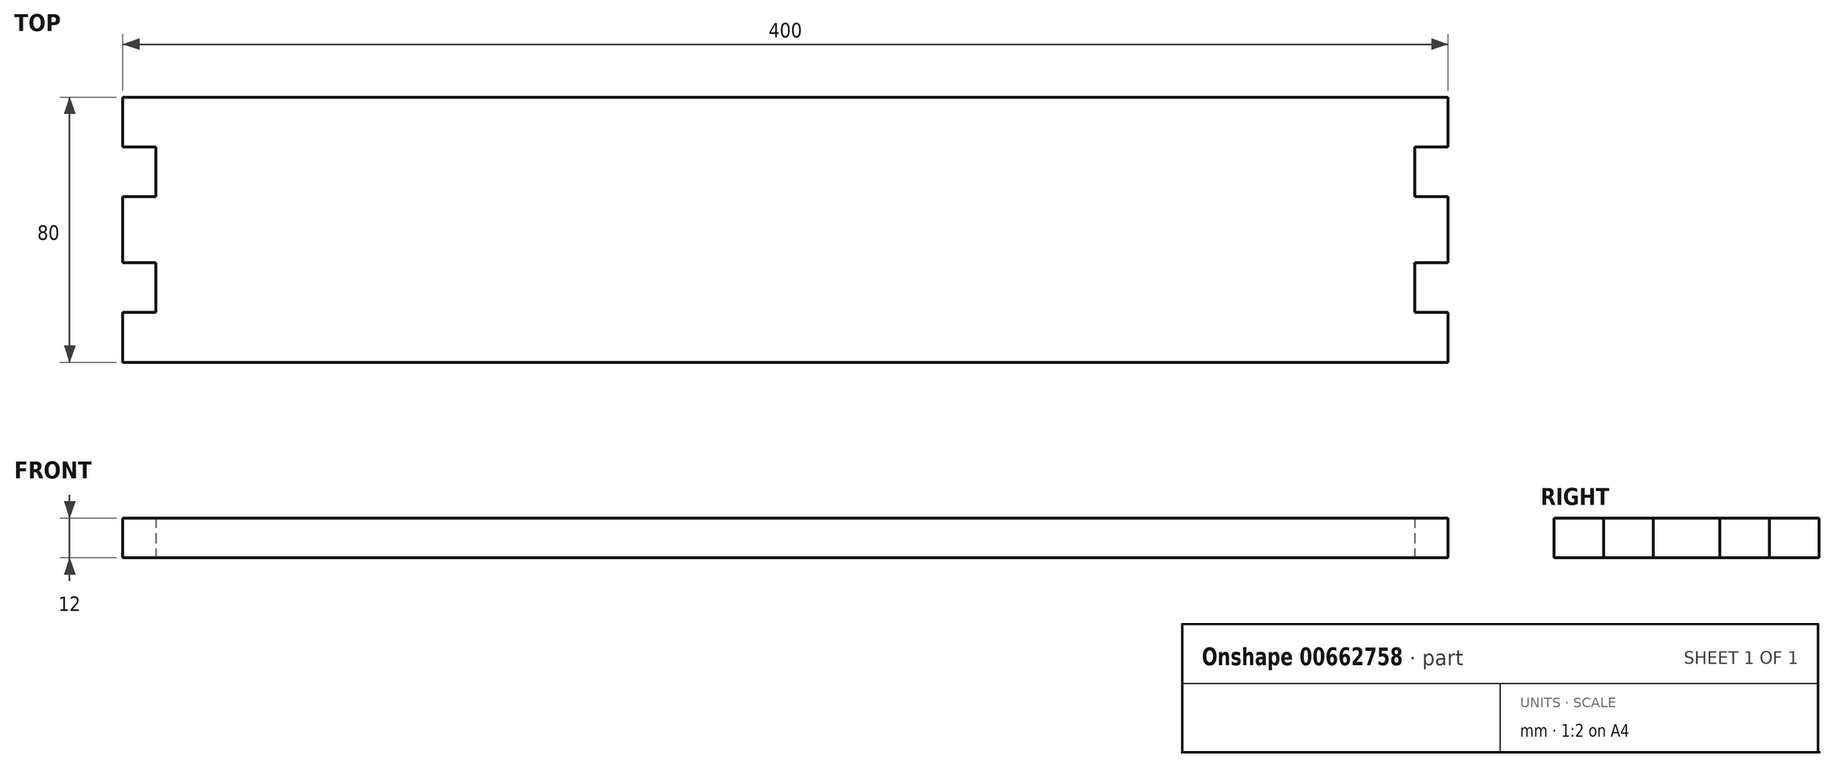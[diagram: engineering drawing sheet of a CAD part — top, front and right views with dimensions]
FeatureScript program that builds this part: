
annotation { "Feature Type Name" : "Feature", "Feature Type Description" : "" }
export const myFeature = defineFeature(function(context is Context, id is Id, definition is map)
    precondition{}
    {
        {
            var Q0;
            Q0=qCreatedBy(makeId("Top.planeOp"),FACE);
            var sketch = newSketch(context, id + "F0", { "sketchPlane" : qUnion([Q0])});
            skLineSegment(sketch, "E0.bottom", {"start": v(200, 40) * mm, "end": v(-200, 40) * mm});
            skLineSegment(sketch, "E0.top", {"start": v(200, -40) * mm, "end": v(-200, -40) * mm});
            skLineSegment(sketch, "E0.left", {"start": v(200, 40) * mm, "end": v(200, -40) * mm});
            skLineSegment(sketch, "E0.right", {"start": v(-200, 40) * mm, "end": v(-200, -40) * mm});
            skPoint(sketch, "E0.middle", {"position": v(0, 0) * mm});
            skLineSegment(sketch, "E1", {"start": v(200, -25) * mm, "end": v(190, -25) * mm});
            skLineSegment(sketch, "E2", {"start": v(190, -25) * mm, "end": v(190, -10) * mm});
            skLineSegment(sketch, "E3", {"start": v(190, -10) * mm, "end": v(200, -10) * mm});
            skLineSegment(sketch, "E4.MirrorCS", {"start": v(200, 25) * mm, "end": v(190, 25) * mm});
            skLineSegment(sketch, "E5.MirrorCS", {"start": v(190, 10) * mm, "end": v(200, 10) * mm});
            skLineSegment(sketch, "E6.MirrorCS", {"start": v(190, 25) * mm, "end": v(190, 10) * mm});
            skLineSegment(sketch, "E7.MirrorCS", {"start": v(-200, -25) * mm, "end": v(-190, -25) * mm});
            skLineSegment(sketch, "E8.MirrorCS", {"start": v(-190, -25) * mm, "end": v(-190, -10) * mm});
            skLineSegment(sketch, "E9.MirrorCS", {"start": v(-190, -10) * mm, "end": v(-200, -10) * mm});
            skLineSegment(sketch, "E10.MirrorCS", {"start": v(-190, 10) * mm, "end": v(-200, 10) * mm});
            skLineSegment(sketch, "E11.MirrorCS", {"start": v(-200, 25) * mm, "end": v(-190, 25) * mm});
            skLineSegment(sketch, "E12.MirrorCS", {"start": v(-190, 25) * mm, "end": v(-190, 10) * mm});
            skSolve(sketch);
        }
        {
            var Q0;
            Q0=makeQuery(id+"F0.imprint","IMPRINT",FACE,{"disambiguationData":[TD([[makeQuery(id+"F0.imprint","IMPRINT",EDGE,{"derivedFrom":sQuery(id+"F0.wireOp",EDGE,"E0.bottom")}),1.0]])]});
            extrude(context, id + "F1", {"entities" : qUnion([Q0]), "endBound" : BoundingType.SYMMETRIC, "depth" : 12 * mm, "offsetDistance" : 25 * mm});
        }
    });
